FCSTD DOCUMENT  (FreeCAD 2024.2R37179 (Git))
Label: model2
License: All rights reserved
LicenseURL: https://en.wikipedia.org/wiki/All_rights_reserved
objects: Sketcher::SketchObject×2, PartDesign::Plane×1, PartDesign::Body×1
note: 4 computed .brp shape members not serialized (recipe doc carries the construction recipe); baked Part::Feature solids carry a one-line shape summary decoded from their .brp

FEATURE [Sketcher::SketchObject] Sketch
  AttachmentSupport = -> [XY_Plane001]
  FullyConstrained = true
  MapMode = 5
  sketch-geometry (9):
    g0: LineSegment StartX=-14 StartY=0 StartZ=0 EndX=-14 EndY=14 EndZ=0
    g1: LineSegment StartX=-14 StartY=14 StartZ=0 EndX=0 EndY=14 EndZ=0
    g2: LineSegment StartX=14 StartY=14 StartZ=0 EndX=0 EndY=14 EndZ=0
    g3: LineSegment StartX=14 StartY=0 StartZ=0 EndX=14 EndY=14 EndZ=0
    g4: LineSegment StartX=-14 StartY=0 StartZ=0 EndX=-12 EndY=0 EndZ=0
    g5: LineSegment StartX=-12 StartY=0 StartZ=0 EndX=-12 EndY=12 EndZ=0
    g6: LineSegment StartX=-12 StartY=12 StartZ=0 EndX=12 EndY=12 EndZ=0
    g7: LineSegment StartX=12 StartY=12 StartZ=0 EndX=12 EndY=0 EndZ=0
    g8: LineSegment StartX=12 StartY=0 StartZ=0 EndX=14 EndY=0 EndZ=0
  constraints (27):
    c: PointOnObject(g0,g-1)
    c: Coincident(g0,g1)
    c: PointOnObject(g1,g-2)
    c: Horizontal(g1)
    c: Vertical(g0)
    c: DistanceX(g1,g1) = 14
    c: Equal(g1,g0)
    c: Coincident(g3,g2)
    c: Horizontal(g2)
    c: Vertical(g3)
    c: Equal(g2,g3)
    c: Coincident(g2,g1)
    c: PointOnObject(g3,g-1)
    c: Coincident(g0,g4)
    c: PointOnObject(g4,g-1)
    c: Coincident(g4,g5)
    c: Vertical(g5)
    c: Coincident(g5,g6)
    c: Horizontal(g6)
    c: Coincident(g6,g7)
    c: PointOnObject(g7,g-1)
    c: Vertical(g7)
    c: Coincident(g7,g8)
    c: Coincident(g8,g3)
    c: Equal(g8,g4)
    c: DistanceX(g4,g4) = 2
    c: DistanceY(g5,g0) = 2
FEATURE [PartDesign::Plane] DatumPlane
  AttachmentOffset = pos=(0,0,50) rot=(0,0,1;0rad)
  AttachmentSupport = -> [XY_Plane001]
  Length = 60
  MapMode = 2
  Placement = pos=(0,0,50) rot=(0,0,1;0rad)
  ResizeMode = 0
  Width = 60
FEATURE [Sketcher::SketchObject] Sketch001
  AttachmentSupport = -> [DatumPlane]
  FullyConstrained = true
  MapMode = 5
  Placement = pos=(0,0,50) rot=(0,0,1;0rad)
  expr: Constraints[21] = 37 / 2
  expr: Constraints[22] = 37 / 2
  expr: Constraints[23] = 37 / 2
  sketch-geometry (8):
    g0: LineSegment StartX=-16.5 StartY=0 StartZ=0 EndX=-16.5 EndY=18.5 EndZ=0
    g1: LineSegment StartX=-16.5 StartY=18.5 StartZ=0 EndX=16.5 EndY=18.5 EndZ=0
    g2: LineSegment StartX=16.5 StartY=18.5 StartZ=0 EndX=16.5 EndY=0 EndZ=0
    g3: LineSegment StartX=16.5 StartY=0 StartZ=0 EndX=18.5 EndY=0 EndZ=0
    g4: LineSegment StartX=18.5 StartY=0 StartZ=0 EndX=18.5 EndY=20.5 EndZ=0
    g5: LineSegment StartX=18.5 StartY=20.5 StartZ=0 EndX=-18.5 EndY=20.5 EndZ=0
    g6: LineSegment StartX=-18.5 StartY=20.5 StartZ=0 EndX=-18.5 EndY=0 EndZ=0
    g7: LineSegment StartX=-18.5 StartY=0 StartZ=0 EndX=-16.5 EndY=0 EndZ=0
  constraints (24):
    c: PointOnObject(g0,g-1)
    c: Vertical(g0)
    c: Coincident(g0,g1)
    c: Horizontal(g1)
    c: Coincident(g1,g2)
    c: PointOnObject(g2,g-1)
    c: Vertical(g2)
    c: Coincident(g2,g3)
    c: PointOnObject(g3,g-1)
    c: Coincident(g3,g4)
    c: Coincident(g4,g5)
    c: Horizontal(g5)
    c: Coincident(g5,g6)
    c: PointOnObject(g6,g-1)
    c: Vertical(g6)
    c: Coincident(g6,g7)
    c: Coincident(g7,g0)
    c: Vertical(g4)
    c: Equal(g7,g3)
    c: DistanceX(g3,g3) = 2
    c: DistanceY(g1,g4) = 2
    c: DistanceX(g-1,g3) = 18.5
    c: DistanceX(g6,g-1) = 18.5
    c: DistanceY(g0,g0) = 18.5
FEATURE [PartDesign::Body] Body001
  Group = -> [Sketch,DatumPlane,Sketch001]
  Origin = -> Origin001
